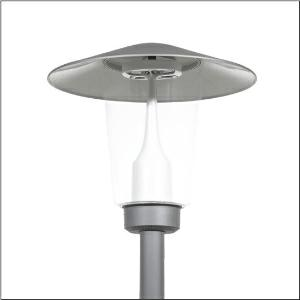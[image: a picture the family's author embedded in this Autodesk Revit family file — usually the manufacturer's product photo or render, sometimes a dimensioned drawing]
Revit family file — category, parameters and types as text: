
# Revit family: pilzleuchte_iq___st1_2a_5xa5235af14h_f6cb
name_source: partatom
category: Lighting Fixtures
units: mm (PartAtom-declared; Revit-internal decimal feet)

## family parameters
Cut with Voids When Loaded = No
Host = Face
Light Source = No
Part Type = Normal
Room Calculation Point = No
Round Connector Dimension = Use Diameter
Shared = No

## types (1)
- --- (1 x LED, 1550 lm, 12.9 W, 2200K)
    Apparent Load = 13 VA
    CIE Flux Codes = 24 61 93 98 100
    Color Rendering = 70
    Color Temperature = 2200K
    Default Elevation = 1800 mm
    Description = Mushroom Luminaire iQ, mast luminaire, Module 540 iQ-SR, primary light control with 3 zone facetted reflector, of plastic, silver coated, highly specular, structured, primary optical cover: cover, of PMMA, transparent, light distribution: ST1.2a, light emission: direct distribution, primary light characteristic: asymmetric, installation type: post-top, LED, High Power LED, rated luminous flux: 1.550lm, luminous efficacy: 120lm/W, light colour: 722, colour temperature: 2200K, control gear: ECG iQ, control: presetting dimming logarithmic, Street-Remote, Auto-Match, Temp-Guard, Lumen-Switch, Night-Set, Smart-Wire, Light-Fading, Desk-Remote (wireless, voltage-free reading and setting of iQ features in the workshop via application-optimized NFC function/RFID function), optimised constant luminous flux control (CLO 2.0), with terminal, 6-pole, max. 2.5mm², mains connection: 230..240V, AC, 50/60Hz, start of lifetime: 13W, end of service life: 13W, reduction: 6W, luminaire housing, upper part, of glass-fibre reinforced polyester, coated, Siteco® metallic grey (DB 702S), diameter: 650mm, height: 586mm, spigot size: d x l = 76 x 70mm (post-top) | with reducer (optional accessory) 60 x 70mm, post-top mast mounting element, of diecast aluminium, coated, Siteco® metallic grey (DB 702S), Module 540 iQ-SR, traffic white (RAL 9016), equipment: standard, protection rating (complete): IP65, insulation class (complete): insulation class II (safety insulation), certification: CE, ENEC, VDE, packaging unit: 1 piece

Light Distribution: ST1.2a
    Height = 586 mm
    Lamp = 1 x LED
    Lamp Light Flux = 1550 lm
    Lamp Power = 12.9 W
    Lamp count = 1
    Length = 650 mm
    Luminous efficacy = 120 lm/W
    Manufacturer = Siteco
    ModVariant = No
    Model = 5XA5235AF14H
    Number of Poles = 1
    OnlyDefault = Yes
    Power Factor = 1
    Product Name = Pilzleuchte iQ | ST1.2a
    Product group = mast luminaire | pylon top
    ProductGroupID = 6100
    Protection Class = Protection class II
    Protection Degree = IP 65
    RLX_Detail_Level = 1
    RLX_Emergency_Light_Flux = 0 lm
    RLX_Emergency_Type = 0
    RLX_Emergency_Type_DB = No
    RlxData = <blob elided: 124261 chars, md5=8c7bb534>
    Socket = socket
    Standby Power = 0 W
    System Light Flux = 1550 lm
    System Power = 13 W
    Type Comments = factory setting: luminous flux: 100 % | dim-lin: 254 | 516 mA
    Type Image = l_1006077.jpg
    URL = http://relux.com
    VarID = @adj_093121
    Voltage = 0 V
    Weight = 0.00 kg
    Width = 0 mm  [stored 0 ft]

note: [stored X ft] marks values corroborated as IEEE doubles in the binary element streams (Revit-internal decimal feet)

## geometry (parser evidence)
native form markers: Blend x4, Sweep x9
no freeform markers — native parametric forms only
